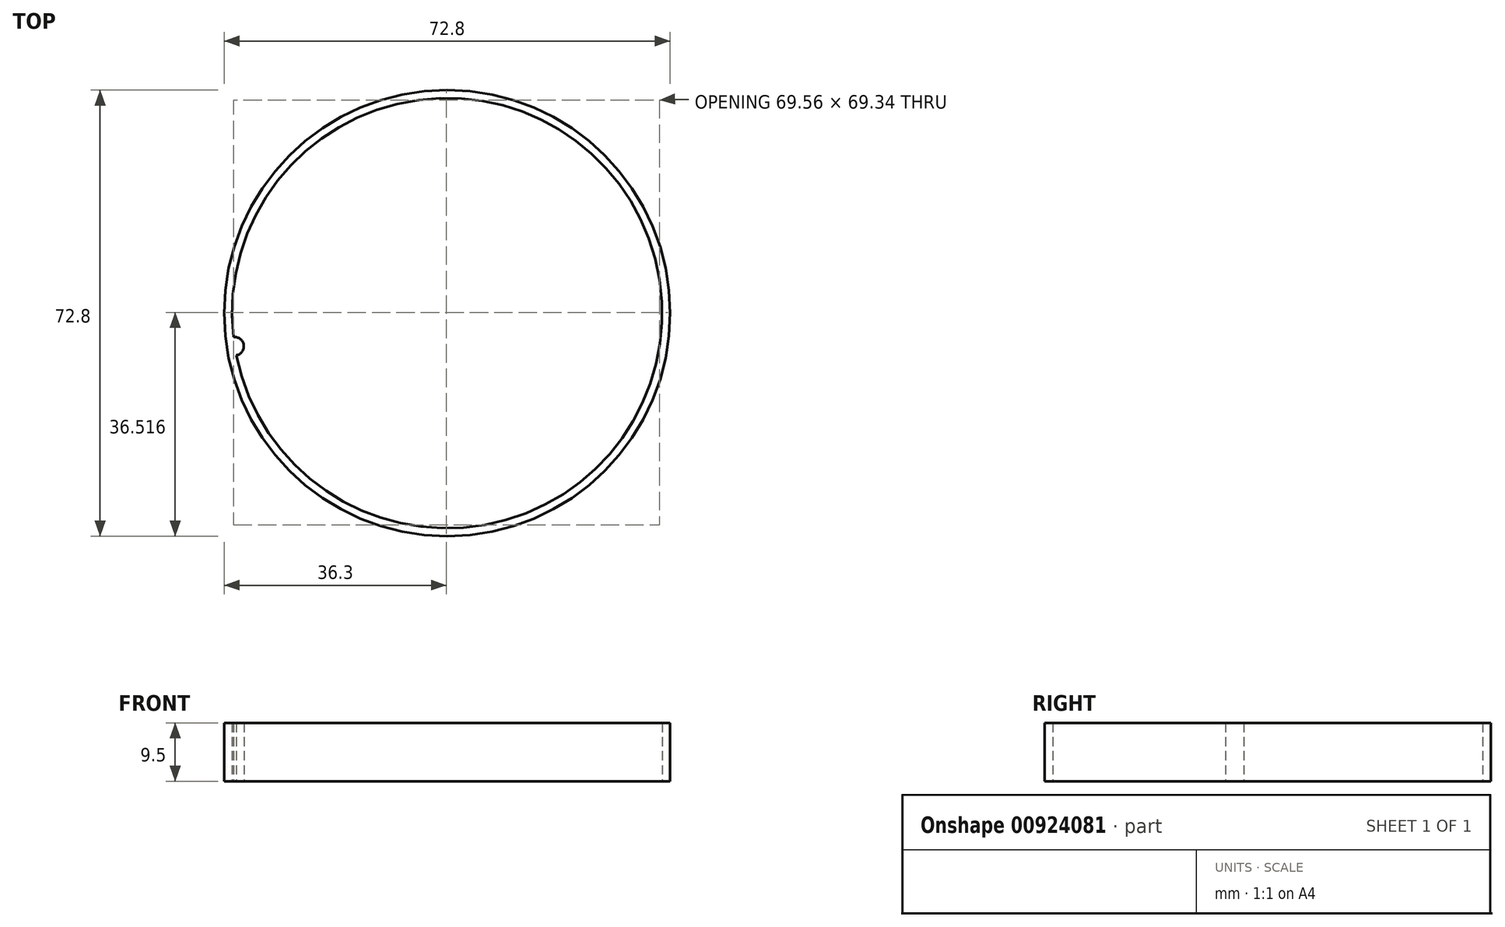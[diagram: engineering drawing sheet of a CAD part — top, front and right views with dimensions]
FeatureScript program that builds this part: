
annotation { "Feature Type Name" : "Feature", "Feature Type Description" : "" }
export const myFeature = defineFeature(function(context is Context, id is Id, definition is map)
    precondition{}
    {
        {
            var Q0;
            Q0=qCreatedBy(makeId("Top.planeOp"),FACE);
            var sketch = newSketch(context, id + "F0", { "sketchPlane" : qUnion([Q0])});
            skArc(sketch, "E0", {"start": v(-34.42, -6.89) * mm, "mid": v(34.68, 5.41) * mm, "end": v(-34.88, -3.93) * mm});
            skCircle(sketch, "E1", {"center": v(0, 0) * mm, "radius": 36.4 * mm});
            skArc(sketch, "E2", {"start": v(-34.42, -6.89) * mm, "mid": v(-33.2, -5.18) * mm, "end": v(-34.88, -3.93) * mm});
            skSolve(sketch);
        }
        {
            var Q0;
            Q0=makeQuery(id+"F0.imprint","IMPRINT",FACE,{"disambiguationData":[TD([[makeQuery(id+"F0.imprint","IMPRINT",EDGE,{"derivedFrom":sQuery(id+"F0.wireOp",EDGE,"E0")}),-1.0]])]});
            extrude(context, id + "F1", {"entities" : qUnion([Q0]), "depth" : 9.5 * mm, "offsetDistance" : 25 * mm});
        }
    });
